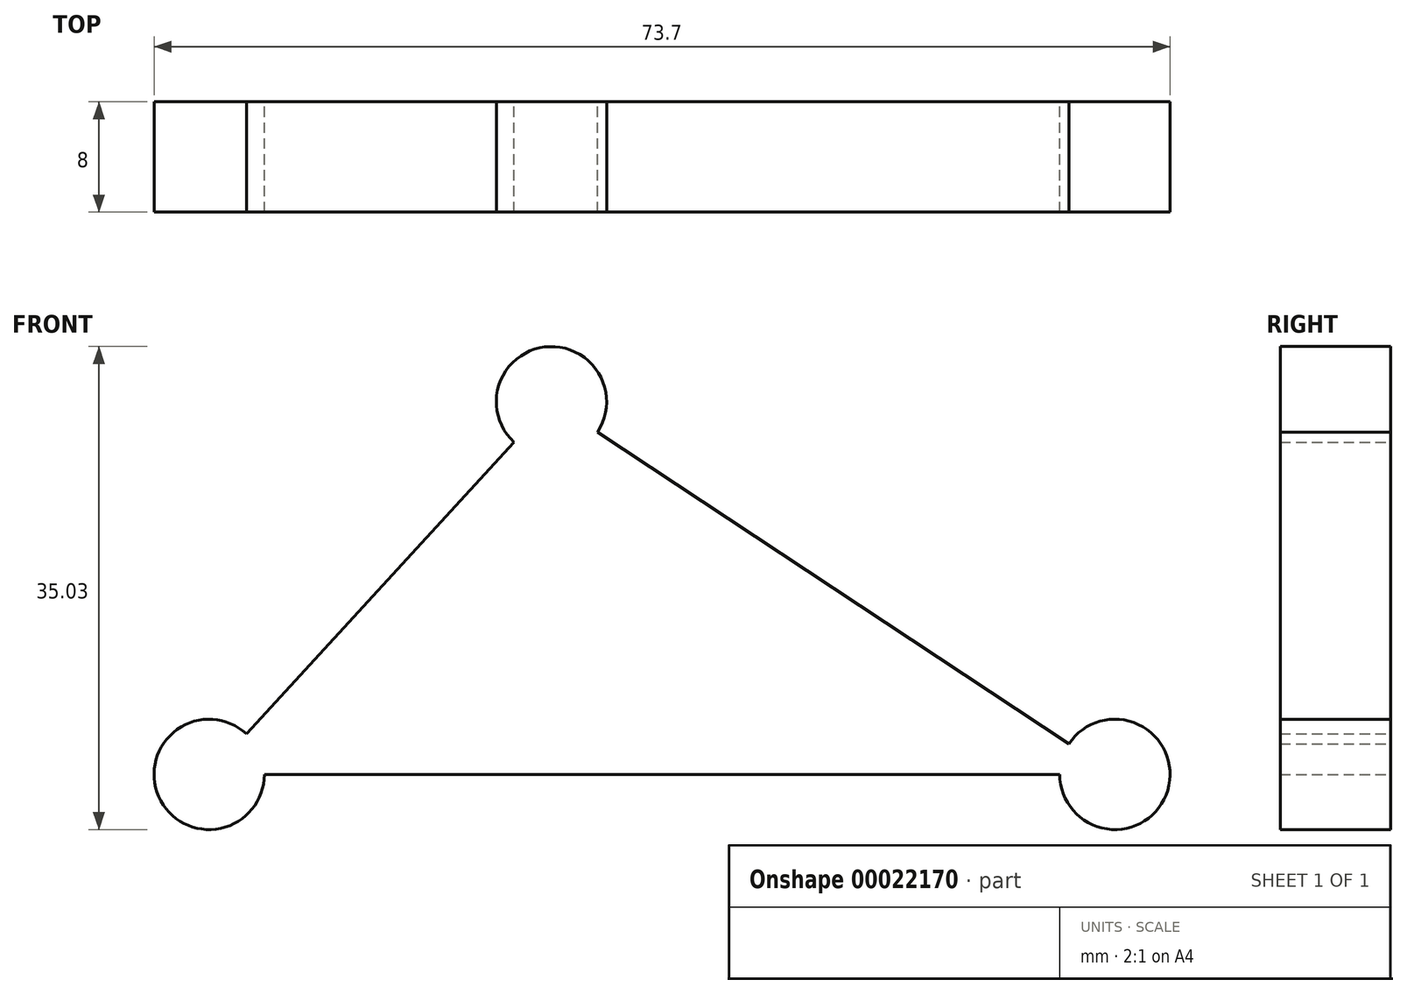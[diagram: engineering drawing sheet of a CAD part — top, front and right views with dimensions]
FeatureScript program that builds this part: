
annotation { "Feature Type Name" : "Feature", "Feature Type Description" : "" }
export const myFeature = defineFeature(function(context is Context, id is Id, definition is map)
    precondition{}
    {
        {
            var Q0;
            Q0=qCreatedBy(makeId("Front.planeOp"),FACE);
            var sketch = newSketch(context, id + "F0", { "sketchPlane" : qUnion([Q0])});
            skLineSegment(sketch, "E0", {"start": v(0, 0) * mm, "end": v(65.7, 0) * mm});
            skLineSegment(sketch, "E1", {"start": v(65.7, 0) * mm, "end": v(24.83, 27.03) * mm});
            skLineSegment(sketch, "E2", {"start": v(24.83, 27.03) * mm, "end": v(0, 0) * mm});
            skCircle(sketch, "E3", {"center": v(24.83, 27.03) * mm, "radius": 4 * mm});
            skCircle(sketch, "E4", {"center": v(65.7, 0) * mm, "radius": 4 * mm});
            skCircle(sketch, "E5", {"center": v(0, 0) * mm, "radius": 4 * mm});
            skSolve(sketch);
        }
        {
            var Q0;
            Q0 = qSketchRegion(id + "F0", true);
            extrude(context, id + "F1", {"entities" : qUnion([Q0]), "depth" : 8 * mm});
        }
    });
